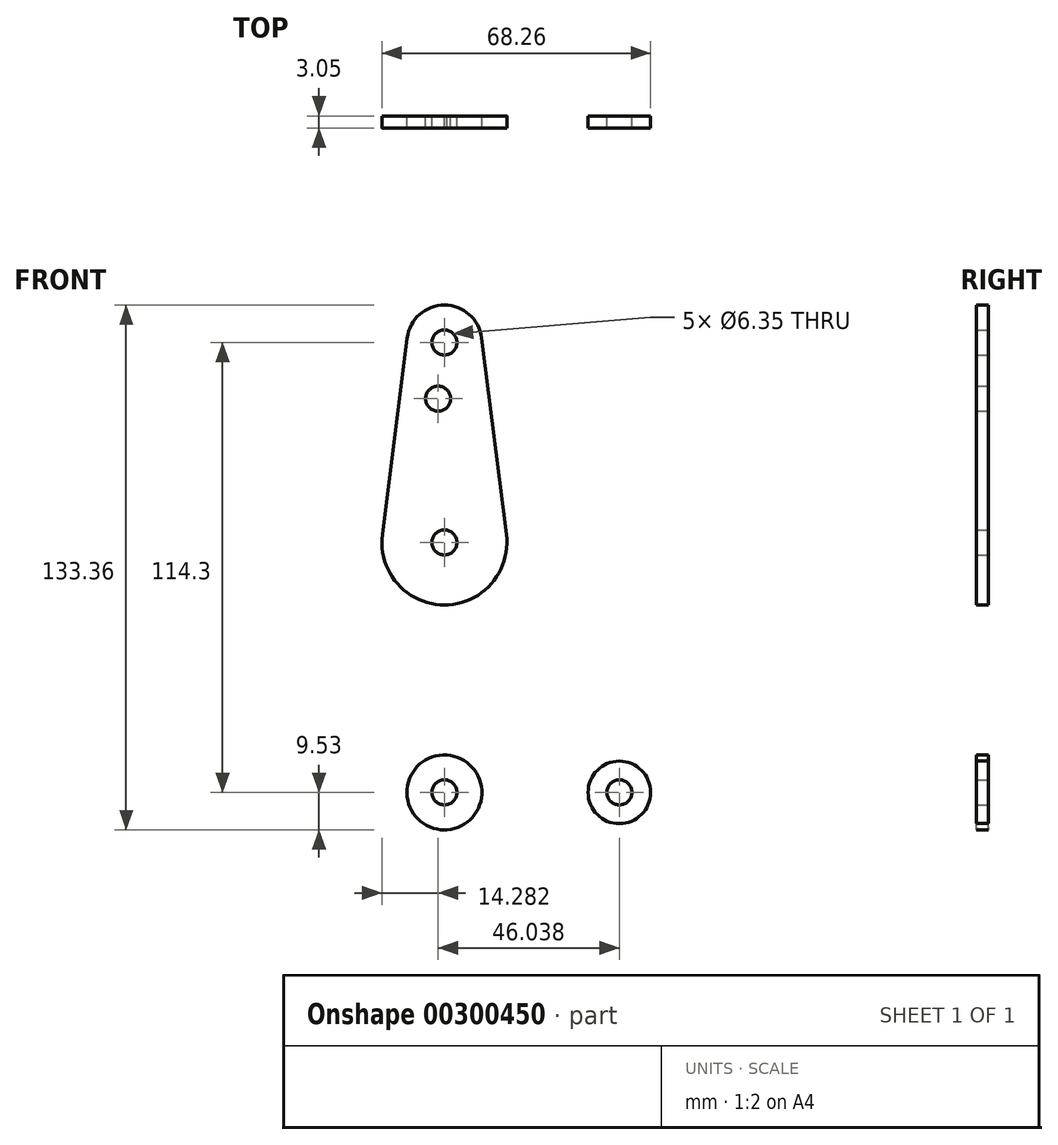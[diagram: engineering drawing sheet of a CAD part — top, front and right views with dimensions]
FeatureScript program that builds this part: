
annotation { "Feature Type Name" : "Feature", "Feature Type Description" : "" }
export const myFeature = defineFeature(function(context is Context, id is Id, definition is map)
    precondition{}
    {
        {
            var Q0;
            Q0=qCreatedBy(makeId("Front.planeOp"),FACE);
            var sketch = newSketch(context, id + "F0", { "sketchPlane" : qUnion([Q0])});
            skLineSegment(sketch, "E0", {"start": v(0, 0) * mm, "end": v(0, 114.3) * mm, "construction": true});
            skCircle(sketch, "E1", {"center": v(0, 0) * mm, "radius": 9.53 * mm});
            skCircle(sketch, "E2", {"center": v(0, 63.5) * mm, "radius": 15.88 * mm});
            skCircle(sketch, "E3", {"center": v(0, 114.3) * mm, "radius": 9.53 * mm});
            skLineSegment(sketch, "E4", {"start": v(0, 0) * mm, "end": v(44.45, 0) * mm, "construction": true});
            skCircle(sketch, "E5", {"center": v(44.45, 0) * mm, "radius": 7.94 * mm});
            skLineSegment(sketch, "E6", {"start": v(-9.45, 115.5) * mm, "end": v(-15.75, 65.48) * mm});
            skLineSegment(sketch, "E7", {"start": v(9.45, 115.5) * mm, "end": v(15.75, 65.48) * mm});
            skLineSegment(sketch, "E8", {"start": v(-15.8, 61.91) * mm, "end": v(-9.57, 0) * mm});
            skLineSegment(sketch, "E9", {"start": v(15.8, 61.91) * mm, "end": v(11.25, 16.66) * mm});
            skLineSegment(sketch, "E10", {"start": v(18.54, 8.44) * mm, "end": v(44.6, 7.94) * mm});
            skLineSegment(sketch, "E11", {"start": v(0, -9.53) * mm, "end": v(44.73, -7.93) * mm});
            skCircle(sketch, "E12", {"center": v(0, 114.3) * mm, "radius": 3.18 * mm});
            skCircle(sketch, "E13", {"center": v(-1.59, 100.03) * mm, "radius": 3.18 * mm});
            skCircle(sketch, "E14", {"center": v(0, 63.5) * mm, "radius": 3.18 * mm});
            skCircle(sketch, "E15", {"center": v(0, 0) * mm, "radius": 3.18 * mm});
            skCircle(sketch, "E16", {"center": v(44.45, 0) * mm, "radius": 3.18 * mm});
            skPoint(sketch, "E17.newPointB", {"position": v(0, 8.8) * mm});
            skArc(sketch, "E17.filletArc", {"start": v(11.25, 16.66) * mm, "mid": v(13.1, 10.96) * mm, "end": v(18.54, 8.44) * mm});
            skSolve(sketch);
        }
        {
            var Q0;
            {var subQ1=sQuery(id+"F0.wireOp",EDGE,"E6");Q0=makeQuery(id+"F0.imprint","IMPRINT",FACE,{"disambiguationData":[TD([[makeQuery(id+"F0.imprint","IMPRINT",EDGE,{"derivedFrom":subQ1}),1.0]])]});}
            var Q1;
            Q1=makeQuery(id+"F0.imprint","IMPRINT",FACE,{"disambiguationData":[TD([[makeQuery(id+"F0.imprint","IMPRINT",EDGE,{"derivedFrom":sQuery(id+"F0.wireOp",EDGE,"E15")}),-1.0]])]});
            var Q2;
            Q2=makeQuery(id+"F0.imprint","IMPRINT",FACE,{"disambiguationData":[TD([[makeQuery(id+"F0.imprint","IMPRINT",EDGE,{"derivedFrom":sQuery(id+"F0.wireOp",EDGE,"E14")}),-1.0]])]});
            var Q3;
            Q3=makeQuery(id+"F0.imprint","IMPRINT",FACE,{"disambiguationData":[TD([[makeQuery(id+"F0.imprint","IMPRINT",EDGE,{"derivedFrom":sQuery(id+"F0.wireOp",EDGE,"E12")}),-1.0]])]});
            var Q4;
            Q4=makeQuery(id+"F0.imprint","IMPRINT",FACE,{"disambiguationData":[TD([[makeQuery(id+"F0.imprint","IMPRINT",EDGE,{"derivedFrom":sQuery(id+"F0.wireOp",EDGE,"E16")}),-1.0]])]});
            extrude(context, id + "F1", {"entities" : qUnion([Q0, Q1, Q2, Q3, Q4]), "depth" : 3.05 * mm});
        }
    });
